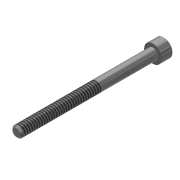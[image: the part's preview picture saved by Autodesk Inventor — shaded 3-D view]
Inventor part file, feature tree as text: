
AUTODESK INVENTOR PART (.ipt)
format: ipt  version: 2013 (Build 170138000, 138)  size: 93,184 bytes
history: native  units: in
note: dims shown in document units (in); Inventor stores cm internally (conversion verified against a paired STEP export)
features: extrude x3, sketch x3, chamfer x1, thread x1
ambient origin geometry x8: Origin, YZ Plane, XZ Plane, XY Plane, X Axis, Y Axis, Z Axis, Center Point
bodies: Solid1 (feature_tree)
feature tree (8):
  extrude  "Extrusion1"  Depth=1.75in TaperAngle=0.0deg
  extrude  "Extrusion2"  Depth=0.138in TaperAngle=0.0deg
  extrude  "Extrusion3"  Depth=0.069in TaperAngle=0.0deg
  chamfer  "Chamfer1"  Distance=0.02in Angle=45.0deg
  thread  "Thread2"  [1 undecoded]
  sketch  "Sketch1"  dims[d0=0.138in d1=1.75in d2=0.0in]
  sketch  "Sketch2"  dims[d3=0.226in d4=0.138in d5=0.0in]
  sketch  "Sketch3"  dims[d6=0.1094in d7=0.069in d8=0.0in d11=0.02in d12=0.125in d13=45.0deg d14=1.0in d15=0.0in]
note: 1 required parameter value undecoded (feature->parameter linkage not recoverable at this tier; creation-order binding heuristic only, values carry confidence <= 0.55)
